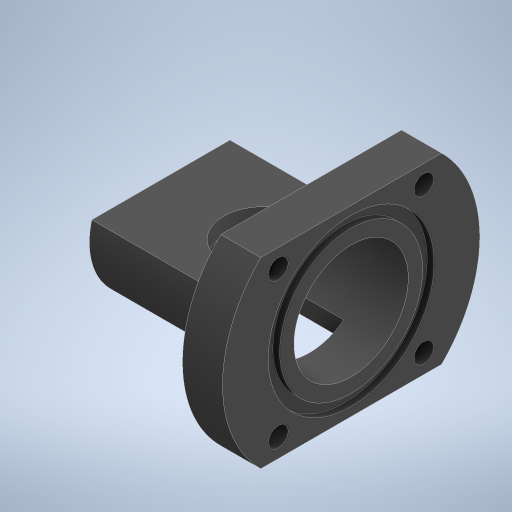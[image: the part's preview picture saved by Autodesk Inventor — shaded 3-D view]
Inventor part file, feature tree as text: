
AUTODESK INVENTOR PART (.ipt)
format: ipt  version: 2023 (Build 270158000, 158)  size: 344,576 bytes
history: native  units: mm
features: sketch x8, extrude x6, other x3, projected_geometry x2, revolve x1, hole x1, pattern_circular x1, reference x1
ambient origin geometry x8: Origin, YZ Plane, XZ Plane, XY Plane, X Axis, Y Axis, Z Axis, Center Point
bodies: Body1 (feature_tree)
feature tree (23):
  revolve  "Revolution2"  [1 undecoded]
  extrude  "Extrusion2"  Depth=1.5mm
  extrude  "Extrusion4"  Depth=45.0mm
  extrude  "Extrusion5"  Depth=15.0mm
  extrude  "Extrusion6"  Depth=16.0mm
  extrude  "Extrusion7"  Depth=10.0mm
  extrude  "Extrusion8"  Depth=10.0mm
  hole  "Hole3"  [1 undecoded]
  pattern_circular  "Circular Pattern2"  [2 undecoded]
  sketch  "Sketch4"  dims[d44=25.0mm d45=1.5mm]
  sketch  "Sketch7"  dims[d46=1.2mm d47=1.5mm]
  sketch  "Sketch10"  dims[d50=90.0deg d53=45.0mm]
  projected_geometry  "Projected Loop2"
  sketch  "Sketch11"  dims[d58=7.0mm d59=15.0mm]
  reference  "Reference2"
  sketch  "Sketch12"  dims[d60=0.0mm d61=16.0mm]
  projected_geometry  "Projected Loop3"
  sketch  "Sketch13"  dims[d62=16.0mm d63=10.0mm]
  sketch  "Sketch14"  dims[d64=10.0mm d65=20.0mm]
  sketch  "Sketch15"  dims[d66=20.0mm d67=0.0mm d72=0.2mm d73=3.0mm d74=26.0mm d75=0.0mm d76=14.0mm d77=0.0mm d78=0.0mm d79=6.0mm d80=6.0mm d81=26.0mm d82=0.0mm d83=20.0mm d84=15.0mm d85=0.0mm d86=2.0mm d87=1.2mm d88=0.0mm d89=18.0mm d90=45.0deg d91=3.4mm d92=6.0mm d93=6.3mm d94=2.0mm d95=90.0deg d96=8.0mm d97=20.594885mm d98=40.0mm d99=360.0deg d69=0.5mm d70=0.872665mm d71=0.5mm]
  parser-record x1  (decoder bookkeeping rows leaked as tree rows — omitted from the tree; the rows remain in map.json)
  other  "ApertureActuator.iam"
  other  "GM1024BY10:1"
note: 4 required parameter values undecoded (feature->parameter linkage not recoverable at this tier; creation-order binding heuristic only, values carry confidence <= 0.55)
note: 1 file-system path scrubbed to <path> (originals preserved in map.json)